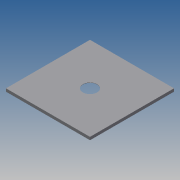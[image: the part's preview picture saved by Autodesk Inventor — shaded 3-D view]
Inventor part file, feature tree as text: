
AUTODESK INVENTOR PART (.ipt)
format: ipt  version: 2014 SP1 (Build 180222100, 222)  size: 138,240 bytes
history: native  units: in
note: dims shown in document units (in); Inventor stores cm internally (conversion verified against a paired STEP export)
features: extrude x3, sketch x3
ambient origin geometry x8: Origin, YZ Plane, XZ Plane, XY Plane, X Axis, Y Axis, Z Axis, Center Point
bodies: Solid1 (feature_tree)
feature tree (6):
  extrude  "Extrusion1"  Depth=34.252in
  extrude  "Extrusion2"  Depth=0.3937in
  extrude  "Extrusion3"  Depth=1.0827in
  sketch  "Sketch1"  dims[d0=34.252in d1=34.252in]
  sketch  "Sketch2"  dims[d2=1.1811in d3=0.0in d4=0.3937in]
  sketch  "Sketch3"  dims[d5=1.0827in d6=0.0in d7=5.8in d8=1.0in d9=0.0in]
